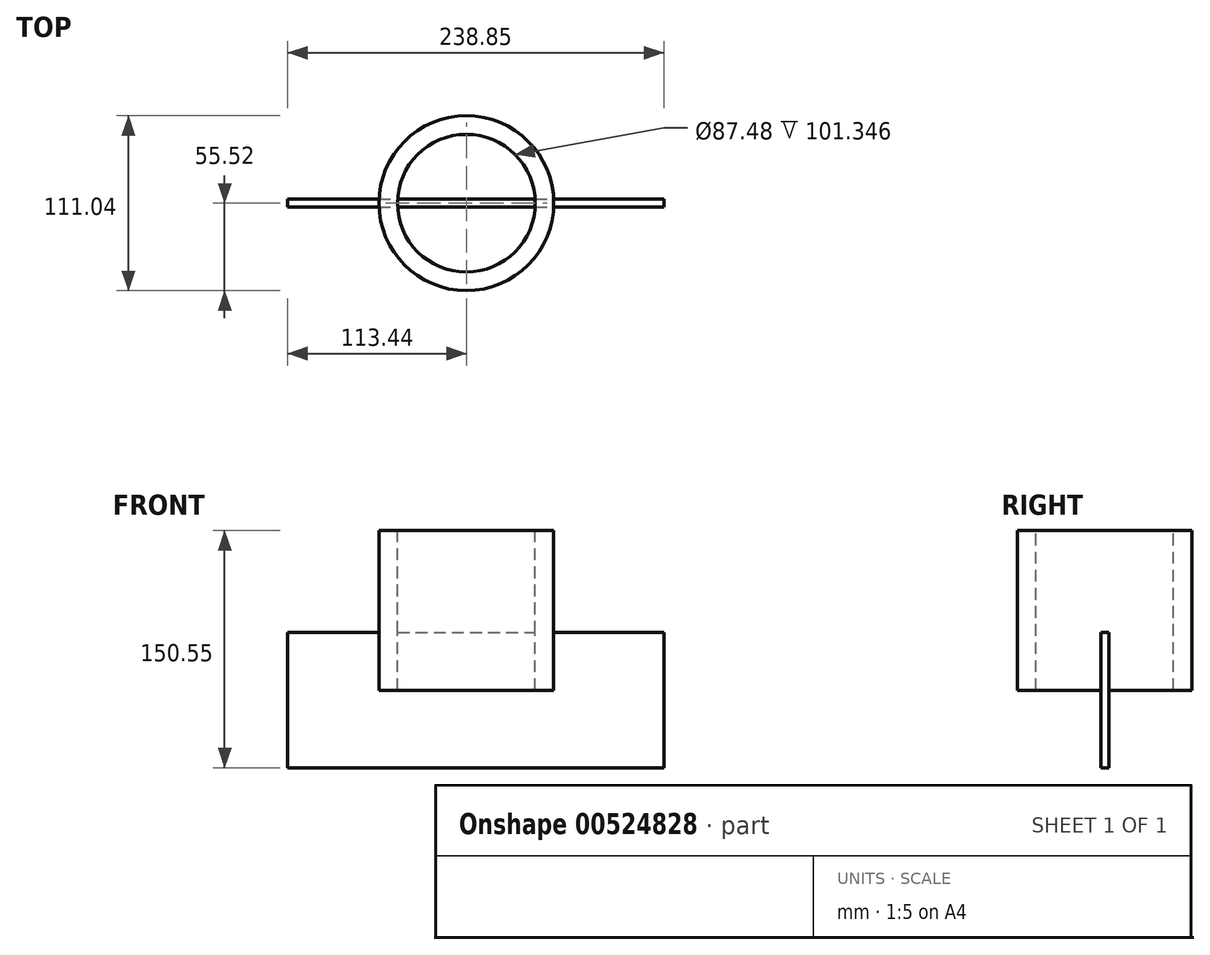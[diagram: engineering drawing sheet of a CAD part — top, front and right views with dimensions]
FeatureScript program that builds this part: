
annotation { "Feature Type Name" : "Feature", "Feature Type Description" : "" }
export const myFeature = defineFeature(function(context is Context, id is Id, definition is map)
    precondition{}
    {
        {
            var Q0;
            Q0=qCreatedBy(makeId("Top.planeOp"),FACE);
            var sketch = newSketch(context, id + "F0", { "sketchPlane" : qUnion([Q0])});
            skCircle(sketch, "E0", {"center": v(0, 0) * mm, "radius": 55.52 * mm});
            skCircle(sketch, "E1", {"center": v(0, 0) * mm, "radius": 43.74 * mm});
            skSolve(sketch);
        }
        {
            var Q0;
            Q0 = qSketchRegion(id + "F0", true);
            extrude(context, id + "F1", {"entities" : qUnion([Q0]), "oppositeDirection" : true, "depth" : 101.35 * mm, "offsetDistance" : 25.4 * mm});
        }
        {
            var Q0;
            Q0=qCreatedBy(makeId("Front.planeOp"),FACE);
            var sketch = newSketch(context, id + "F2", { "sketchPlane" : qUnion([Q0])});
            skLineSegment(sketch, "E2.bottom", {"start": v(-113.44, -64.7) * mm, "end": v(125.41, -64.7) * mm});
            skLineSegment(sketch, "E2.top", {"start": v(-113.44, -150.55) * mm, "end": v(125.41, -150.55) * mm});
            skLineSegment(sketch, "E2.left", {"start": v(-113.44, -64.7) * mm, "end": v(-113.44, -150.55) * mm});
            skLineSegment(sketch, "E2.right", {"start": v(125.41, -64.7) * mm, "end": v(125.41, -150.55) * mm});
            skSolve(sketch);
        }
        {
            var Q0;
            Q0 = qSketchRegion(id + "F2", true);
            extrude(context, id + "F3", {"entities" : qUnion([Q0]), "operationType" : NewBodyOperationType.ADD, "depth" : 2.54 * mm, "offsetDistance" : 25.4 * mm, "hasSecondDirection" : true, "secondDirectionOppositeDirection" : true, "secondDirectionDepth" : 2.54 * mm});
        }
    });
